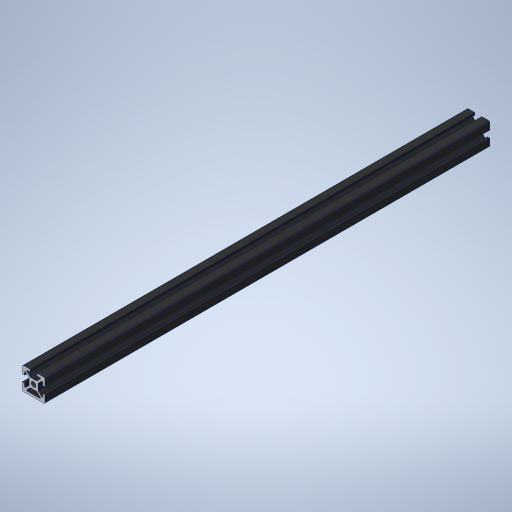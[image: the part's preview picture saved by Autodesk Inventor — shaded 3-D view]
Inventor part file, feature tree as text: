
AUTODESK INVENTOR PART (.ipt)
format: ipt  version: 2024 (Build 280153000, 153)  size: 372,224 bytes
history: native  units: mm
features: other x7, thread x2, sketch x2, extrude x1, hole x1
ambient origin geometry x8: Origin, YZ Plane, XZ Plane, XY Plane, X Axis, Y Axis, Z Axis, Center Point
bodies: Solid1 (feature_tree)
feature tree (13):
  extrude  "Extrusion1"  TaperAngle=0.0deg  [1 undecoded]
  hole  "Hole1"  [1 undecoded]
  other  "C1_XY"
  other  "C1_YZ"
  other  "C1_ZX"
  other  "C1_X"
  other  "C1_Y"
  other  "C1_Z"
  other  "C1_Center"
  thread  "Thread1"  [1 undecoded]
  thread  "Thread2"  [1 undecoded]
  sketch  "Sketch_63"  dims[d2=4.2mm d3=6.0mm d4=4.0mm d5=2.0mm d6=90.0deg d7=440.0mm d8=0.0mm d9=0.0mm d10=10.0mm d11=0.0mm d12=10.0mm d13=0.0mm]
  sketch  "Sketch2"  dims[d0=393.0mm d1=0.0mm]
note: 4 required parameter values undecoded (feature->parameter linkage not recoverable at this tier; creation-order binding heuristic only, values carry confidence <= 0.55)
